# Revit family: Plumbing_Fixtures-Oasis-Drinking_Fountain_Vandal_Resistant_Split_Level
name_source: partatom
category: Plumbing Fixtures
units: mm (PartAtom-declared; Revit-internal decimal feet)

## family parameters
Cut with Voids When Loaded = Yes
Host = Face
OmniClass Number = 23.65.70.14.11
OmniClass Title = Drinking Fountains/Coolers
Part Type = Normal
Room Calculation Point = No
Round Connector Dimension = Use Diameter
Shared = No

## types (8) — shared parameters
Accessory Material = Plastic - Oasis International - Gray
Assembly Code = D2010800
CW Connection = Yes
Cold Water Connection Diameter = 0"
Default Elevation = 1' - 1 9/32"
Depth = 1' - 6 5/8"
Flow Rate = 8 GPH
Frequency = 60 Hz
HW Connection = No
Height = 2' - 0 29/32"
Instruction Sheet Link = https://www.oasiscoolers.com
Keynote = 22 40 00.A1
Load Classification = Power
Manufacturer = OASIS International
Manufacturer Fax Number = 1-(614) 322-2529
Product Documentation Link = https://www.oasiscoolers.com
Product Page URL = https://www.oasiscoolers.com
URL = https://www.oasiscoolers.com
Vent Connection = No
Version = 2021 - v1.0a
Voltage = 115 V
Voltage Comment = 115 Volts, 60 Hz
Warranty URL = https://www.oasiscoolers.com
Waste Connection = Yes
Waste Water Connection Diameter = 0' - 1 1/4"
Water Pressure = 60.00 psi
Water Pressure Range = 20  - 100 PSI
Width = 2' - 11 1/4"
zero-valued in all types: Cost

## per-type parameters (varying)
| type | Cabinet Finish | Chilling Option | Description | Filter Option | Finish | Full Load Current | Model | Product Name | Rated Watts | Weight |
| PGV8ACSL-STL | Metal - Oasis International - Brushed Stainless Steel | Delivers 8.0 gallons of chilled drinking water per hour | Refrigerated Fountain | Option to add Filtration | Metal - Oasis International - Brushed Stainless Steel | 5 A | PGV8ACSL 504528 | Vandal Resistant, BI-level Versacooler II, Refrigerated | 460 W | 94 lb |
| PGVACSL-STL | Metal - Oasis International - Brushed Stainless Steel | Non-Refrigerated Fountain | Non-Refrigerated Fountain | Option to add Filtration | Metal - Oasis International - Brushed Stainless Steel | 0 A | PGVACSL 506239 | Vandal Resistant, BI-level Versacooler II, Non-Refrigerated | 0 W | 64 lb |
| PGVF8ACSL-STL | Metal - Oasis International - Brushed Stainless Steel | Delivers 8.0 gallons of chilled drinking water per hour | Refrigerated Fountain | VersaFilter for taste, odor, lead and chlorine reduction | Metal - Oasis International - Brushed Stainless Steel | 4 A | PGVF8ACSL 506113 | Filtered Vandal Resistant, BI-level Versacooler II, Refrigerated | 460 W | 95 lb |
| PGVFACSL-STL | Metal - Oasis International - Brushed Stainless Steel | Non-Refrigerated Fountain | Non-Refrigerated Fountain | VersaFilter for taste, odor, lead and chlorine reduction | Metal - Oasis International - Brushed Stainless Steel | 0 A | PGVF8ACSL 506113 | Vandal Resistant, BI-level Versacooler II, Non-Refrigerated | 0 W | 65 lb |
| PGV8ACSL-CHR | Metal - Oasis International - Chrome Plated Brass | Delivers 8.0 gallons of chilled drinking water per hour | Refrigerated Fountain | Option to add Filtration | Metal - Oasis International - Chrome Plated Brass | 5 A | PGV8ACSL 036700-001 | Vandal Resistant, BI-level Versacooler II, Refrigerated | 460 W | 94 lb |
| PGVACSL-CHR | Metal - Oasis International - Chrome Plated Brass | Non-Refrigerated Fountain | Non-Refrigerated Fountain | Option to add Filtration | Metal - Oasis International - Chrome Plated Brass | 0 A | PGVACSL 506239 | Vandal Resistant, BI-level Versacooler II, Non-Refrigerated | 0 W | 64 lb |
| PGVF8ACSL-CHR | Metal - Oasis International - Chrome Plated Brass | Delivers 8.0 gallons of chilled drinking water per hour | Refrigerated Fountain | VersaFilter for taste, odor, lead and chlorine reduction | Metal - Oasis International - Chrome Plated Brass | 4 A | PGVF8ACSL 036700-001 | Filtered Vandal Resistant, BI-level Versacooler II, Refrigerated | 460 W | 95 lb |
| PGVFACSL-CHR | Metal - Oasis International - Chrome Plated Brass | Non-Refrigerated Fountain | Non-Refrigerated Fountain | VersaFilter for taste, odor, lead and chlorine reduction | Metal - Oasis International - Chrome Plated Brass | 0 A | PGVF8ACSL 036700-001 | Vandal Resistant, BI-level Versacooler II, Non-Refrigerated | 0 W | 65 lb |

## geometry (parser evidence)
native form markers: Sweep x2
no freeform markers — native parametric forms only
